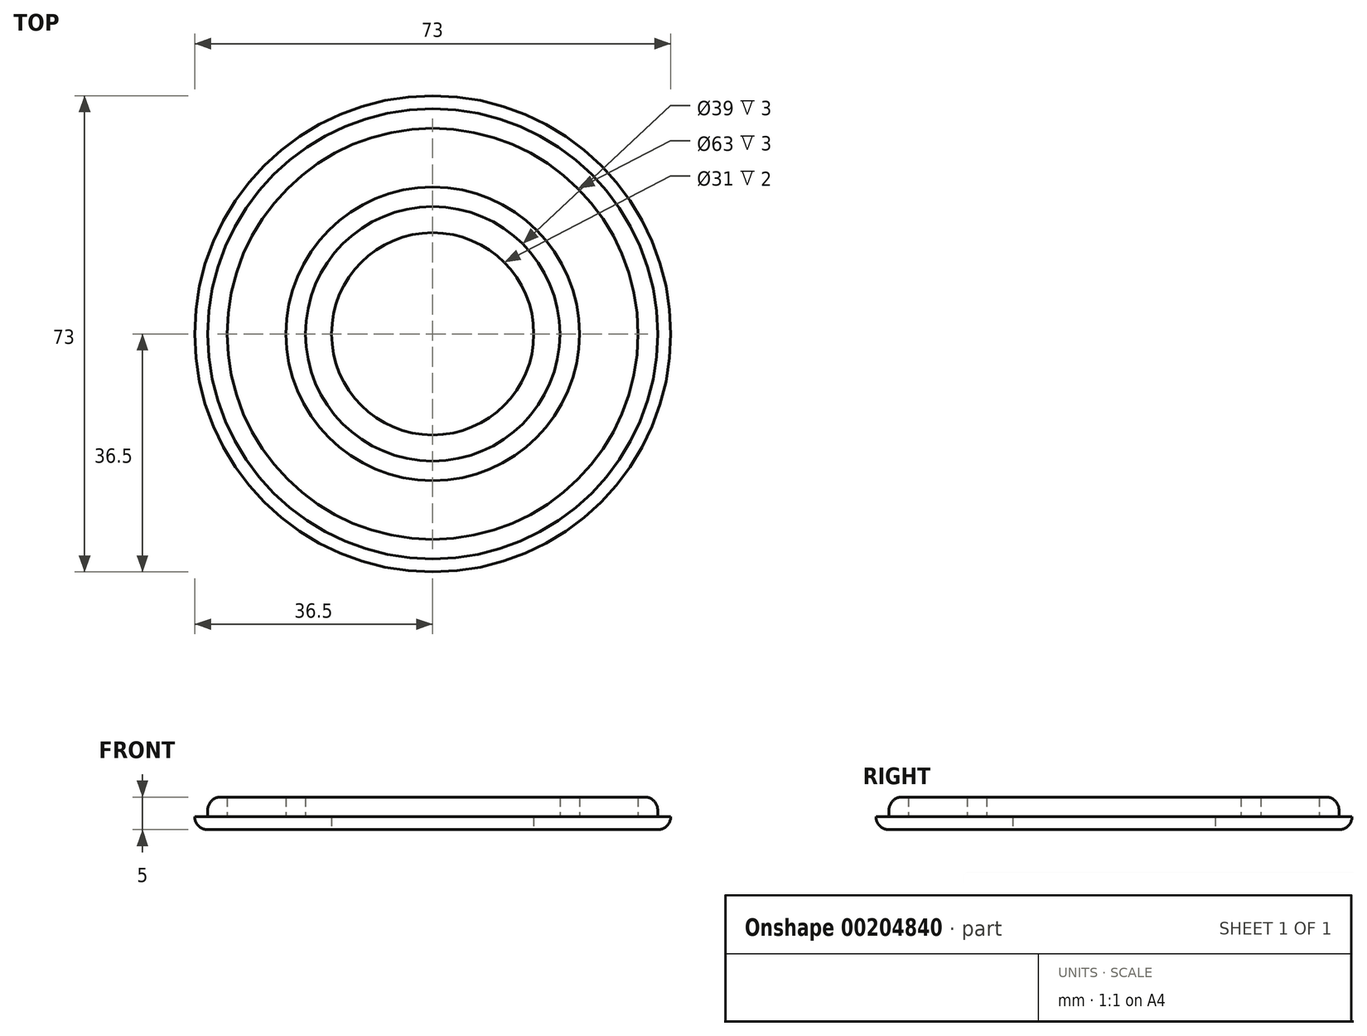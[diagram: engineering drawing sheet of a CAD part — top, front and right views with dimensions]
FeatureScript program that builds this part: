
annotation { "Feature Type Name" : "Feature", "Feature Type Description" : "" }
export const myFeature = defineFeature(function(context is Context, id is Id, definition is map)
    precondition{}
    {
        {
            var Q0;
            Q0=qCreatedBy(makeId("Top.planeOp"),FACE);
            var sketch = newSketch(context, id + "F0", { "sketchPlane" : qUnion([Q0])});
            skCircle(sketch, "E0", {"center": v(0, 0) * mm, "radius": 19.5 * mm});
            skCircle(sketch, "E1", {"center": v(0, 0) * mm, "radius": 31.5 * mm});
            skCircle(sketch, "E2.0", {"center": v(0, 0) * mm, "radius": 34.5 * mm});
            skCircle(sketch, "E3.0", {"center": v(0, 0) * mm, "radius": 36.5 * mm});
            skCircle(sketch, "E4.0", {"center": v(0, 0) * mm, "radius": 15.5 * mm});
            skCircle(sketch, "E5.0", {"center": v(0, 0) * mm, "radius": 22.5 * mm});
            skSolve(sketch);
        }
        {
            var Q0;
            Q0=makeQuery(id+"F0.imprint","IMPRINT",FACE,{"disambiguationData":[TD([[makeQuery(id+"F0.imprint","IMPRINT",EDGE,{"derivedFrom":sQuery(id+"F0.wireOp",EDGE,"E2.0")}),-1.0]])]});
            var Q1;
            Q1=makeQuery(id+"F0.imprint","IMPRINT",FACE,{"disambiguationData":[TD([[makeQuery(id+"F0.imprint","IMPRINT",EDGE,{"derivedFrom":sQuery(id+"F0.wireOp",EDGE,"E1")}),-1.0]])]});
            var Q2;
            Q2=makeQuery(id+"F0.imprint","IMPRINT",FACE,{"disambiguationData":[TD([[makeQuery(id+"F0.imprint","IMPRINT",EDGE,{"derivedFrom":sQuery(id+"F0.wireOp",EDGE,"E1")}),1.0]])]});
            var Q3;
            Q3=makeQuery(id+"F0.imprint","IMPRINT",FACE,{"disambiguationData":[TD([[makeQuery(id+"F0.imprint","IMPRINT",EDGE,{"derivedFrom":sQuery(id+"F0.wireOp",EDGE,"E0")}),-1.0]])]});
            extrude(context, id + "F1", {"entities" : qUnion([Q0, Q1, Q2, Q3]), "depth" : 2 * mm});
        }
        {
            var Q0;
            Q0=makeQuery(id+"F0.imprint","IMPRINT",FACE,{"disambiguationData":[TD([[makeQuery(id+"F0.imprint","IMPRINT",EDGE,{"derivedFrom":sQuery(id+"F0.wireOp",EDGE,"E0")}),-1.0]])]});
            var Q1;
            Q1=makeQuery(id+"F0.imprint","IMPRINT",FACE,{"disambiguationData":[TD([[makeQuery(id+"F0.imprint","IMPRINT",EDGE,{"derivedFrom":sQuery(id+"F0.wireOp",EDGE,"E1")}),-1.0]])]});
            extrude(context, id + "F2", {"entities" : qUnion([Q0, Q1]), "operationType" : NewBodyOperationType.ADD, "depth" : 5 * mm});
        }
        {
            var Q0;
            Q0=makeQuery(id+"F1.opExtrude","CAP_EDGE",EDGE,{"disambiguationData":[OSD([sQuery(id+"F0.wireOp",EDGE,"E3.0")])],"isStart":true});
            fillet(context, id + "F3", {"entities" : qUnion([Q0]), "radius" : 2 * mm, "tangentPropagation" : true, "allowEdgeOverflow" : false});
        }
        {
            var Q0;
            Q0=makeQuery(id+"F2.opExtrude","CAP_EDGE",EDGE,{"disambiguationData":[OSD([sQuery(id+"F0.wireOp",EDGE,"E2.0")])],"isStart":false});
            fillet(context, id + "F4", {"entities" : qUnion([Q0]), "radius" : 2 * mm, "tangentPropagation" : true, "allowEdgeOverflow" : false});
        }
        {
            var Q0;
            Q0=makeQuery(id+"F0.imprint","IMPRINT",FACE,{"disambiguationData":[TD([[makeQuery(id+"F0.imprint","IMPRINT",EDGE,{"derivedFrom":sQuery(id+"F0.wireOp",EDGE,"E0")}),1.0]])]});
            extrude(context, id + "F5", {"entities" : qUnion([Q0]), "operationType" : NewBodyOperationType.ADD, "depth" : 2 * mm});
        }
    });
